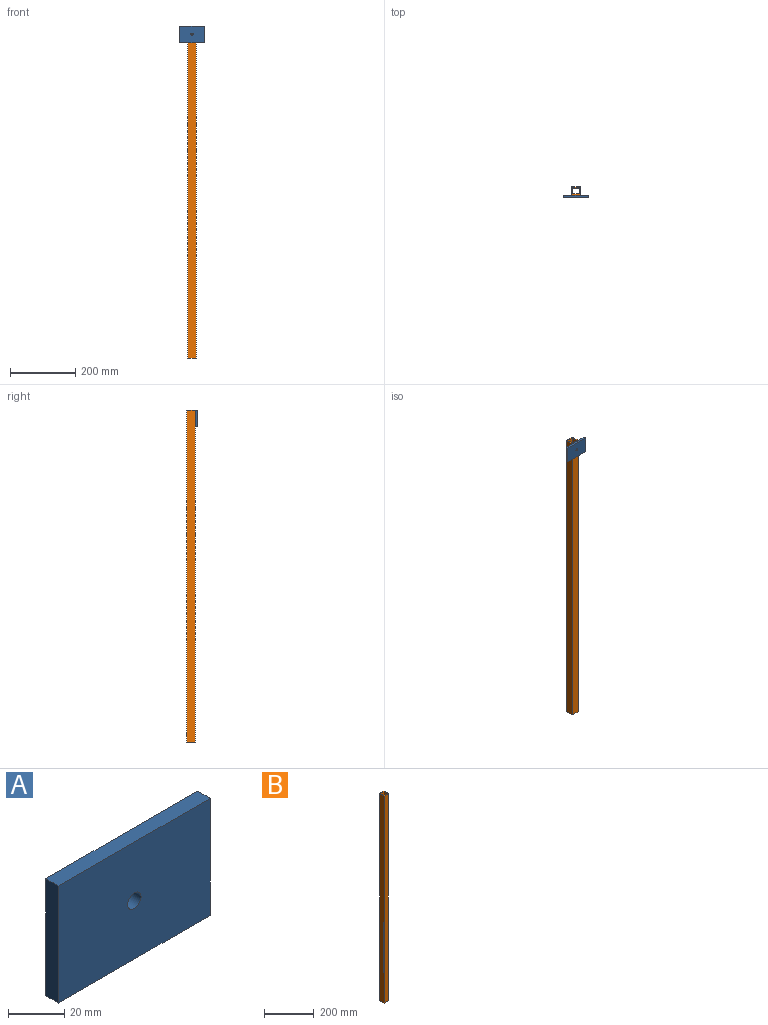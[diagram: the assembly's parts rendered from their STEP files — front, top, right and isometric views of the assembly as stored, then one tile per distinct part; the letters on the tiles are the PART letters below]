
ASSEMBLY  parts=2 mates=1
PART A: 7 faces, bbox 76.2x6.4x50.8 mm
  f0: plane 50.8x6.35mm, normal (1,0,0), area 322.6mm2, adj f1,f3,f4,f5
  f1: plane 76.2x6.35mm, normal (0,0,1), area 483.9mm2, adj f0,f2,f4,f5
  f2: plane 50.8x6.35mm, normal (-1,0,0), area 322.6mm2, adj f1,f3,f4,f5
  f3: plane 76.2x6.35mm, normal (0,0,-1), area 483.9mm2, adj f0,f2,f4,f5
  f4: plane 76.2x50.8mm, normal (0,-1,0), area 3835.1mm2, adj f0,f1,f2,f3,f6
  f5: plane 76.2x50.8mm, normal (0,1,0), area 3835.1mm2, adj f0,f1,f2,f3,f6
  f6: cylinder r=3.38mm len=6.76mm, axis (0,-1,0), area 134.8mm2, adj f4,f5
PART B: 11 faces, bbox 25.4x25.4x1016 mm
  f0: plane 25.4x25.4mm, normal (0,0,1), area 287.9mm2, adj f2,f3,f4,f5,f6,f7,f8,f9
  f1: plane 25.4x25.4mm, normal (0,0,-1), area 287.9mm2, adj f2,f3,f4,f5,f6,f7,f8,f9
  f2: plane 1016x25.4mm, normal (1,0,0), area 25806.4mm2, adj f0,f1,f4,f5
  f3: plane 1016x25.4mm, normal (-1,0,0), area 25806.4mm2, adj f0,f1,f4,f5
  f4: plane 1016x25.4mm, normal (0,-1,0), area 25806.4mm2, adj f0,f1,f2,f3
  f5: plane 1016x25.4mm, normal (0,1,0), area 25785.9mm2, adj f0,f1,f2,f3,f10
  f6: plane 1016x18.75mm, normal (-1,0,0), area 19051.8mm2, adj f0,f1,f7,f9
  f7: plane 1016x19.05mm, normal (0,-1,0), area 19334.3mm2, adj f0,f1,f6,f8,f10
  f8: plane 1016x18.75mm, normal (1,0,0), area 19051.8mm2, adj f0,f1,f7,f9
  f9: plane 1016x19.05mm, normal (0,1,0), area 19354.8mm2, adj f0,f1,f6,f8
  f10: cylinder r=2.55mm len=5.11mm, axis (0,1,0), area 50.9mm2, adj f5,f7
PLACE A t=(-45.44,-36.93,434.55)mm
PLACE B t=(-45.44,-11.53,-48.05)mm
MATE fastened A.f5 <-> B.f4  axis (0,1,0) through (-45.44,-36.93,459.95)mm
